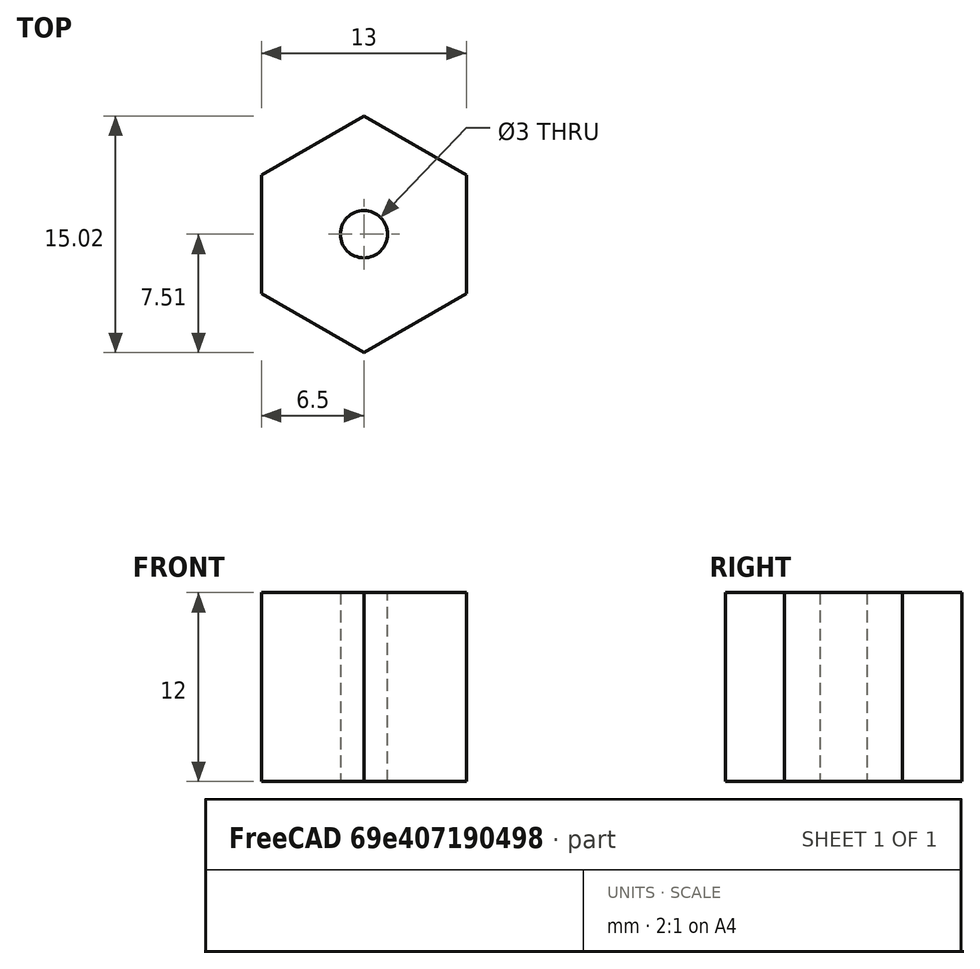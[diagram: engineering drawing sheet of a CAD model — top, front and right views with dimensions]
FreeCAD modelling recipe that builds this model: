
FCSTD DOCUMENT  (FreeCAD 0.19R)
Label: Support_Alim
License: Creative Commons Attribution-NonCommercial
LicenseURL: http://creativecommons.org/licenses/by-nc/4.0/
objects: Sketcher::SketchObject×1, PartDesign::Pad×1, PartDesign::Body×1
note: 4 computed .brp shape members not serialized (recipe doc carries the construction recipe); baked Part::Feature solids carry a one-line shape summary decoded from their .brp

FEATURE [Sketcher::SketchObject] Sketch
  FullyConstrained = true
  MapMode = 5
  Support = -> [XY_Plane]
  sketch-geometry (8):
    g0: LineSegment StartX=6.5 StartY=-3.75278 StartZ=0 EndX=6.5 EndY=3.75278 EndZ=0
    g1: LineSegment StartX=6.5 StartY=3.75278 StartZ=0 EndX=-9e-16 EndY=7.50555 EndZ=0
    g2: LineSegment StartX=-9e-16 StartY=7.50555 StartZ=0 EndX=-6.5 EndY=3.75278 EndZ=0
    g3: LineSegment StartX=-6.5 StartY=3.75278 StartZ=0 EndX=-6.5 EndY=-3.75278 EndZ=0
    g4: LineSegment StartX=-6.5 StartY=-3.75278 StartZ=0 EndX=0 EndY=-7.50555 EndZ=0
    g5: LineSegment StartX=0 StartY=-7.50555 StartZ=0 EndX=6.5 EndY=-3.75278 EndZ=0
    g6: Circle CenterX=0 CenterY=0 CenterZ=0 NormalX=0 NormalY=0 NormalZ=1 AngleXU=0 Radius=7.50555
    g7: Circle CenterX=0 CenterY=0 CenterZ=0 NormalX=0 NormalY=0 NormalZ=1 AngleXU=0 Radius=1.5
  constraints (18):
    c: Coincident(g0,g1)
    c: Coincident(g1,g2)
    c: Coincident(g2,g3)
    c: Coincident(g3,g4)
    c: Coincident(g4,g5)
    c: Coincident(g5,g0)
    c: Equal(g0, g1-g5) x5
    c: PointOnObject(g0,g6)
    c: PointOnObject(g1,g6)
    c: PointOnObject(g2,g6)
    c: PointOnObject(g3,g6)
    c: PointOnObject(g4,g6)
    c: PointOnObject(g5,g6)
    c: Coincident(g6,g-1)
    c: Vertical(g0)
    c: Distance(g0,g2) = 13
    c: Coincident(g7,g-1)
    c: Diameter(g7) = 3
FEATURE [PartDesign::Pad] Pad
  Direction = (1,1,1)
  Length = 12
  Length2 = 100
  Profile = -> Sketch
  Type = 0
FEATURE [PartDesign::Body] Body
  Group = -> [Sketch,Pad]
  Origin = -> Origin
  Tip = -> Pad
